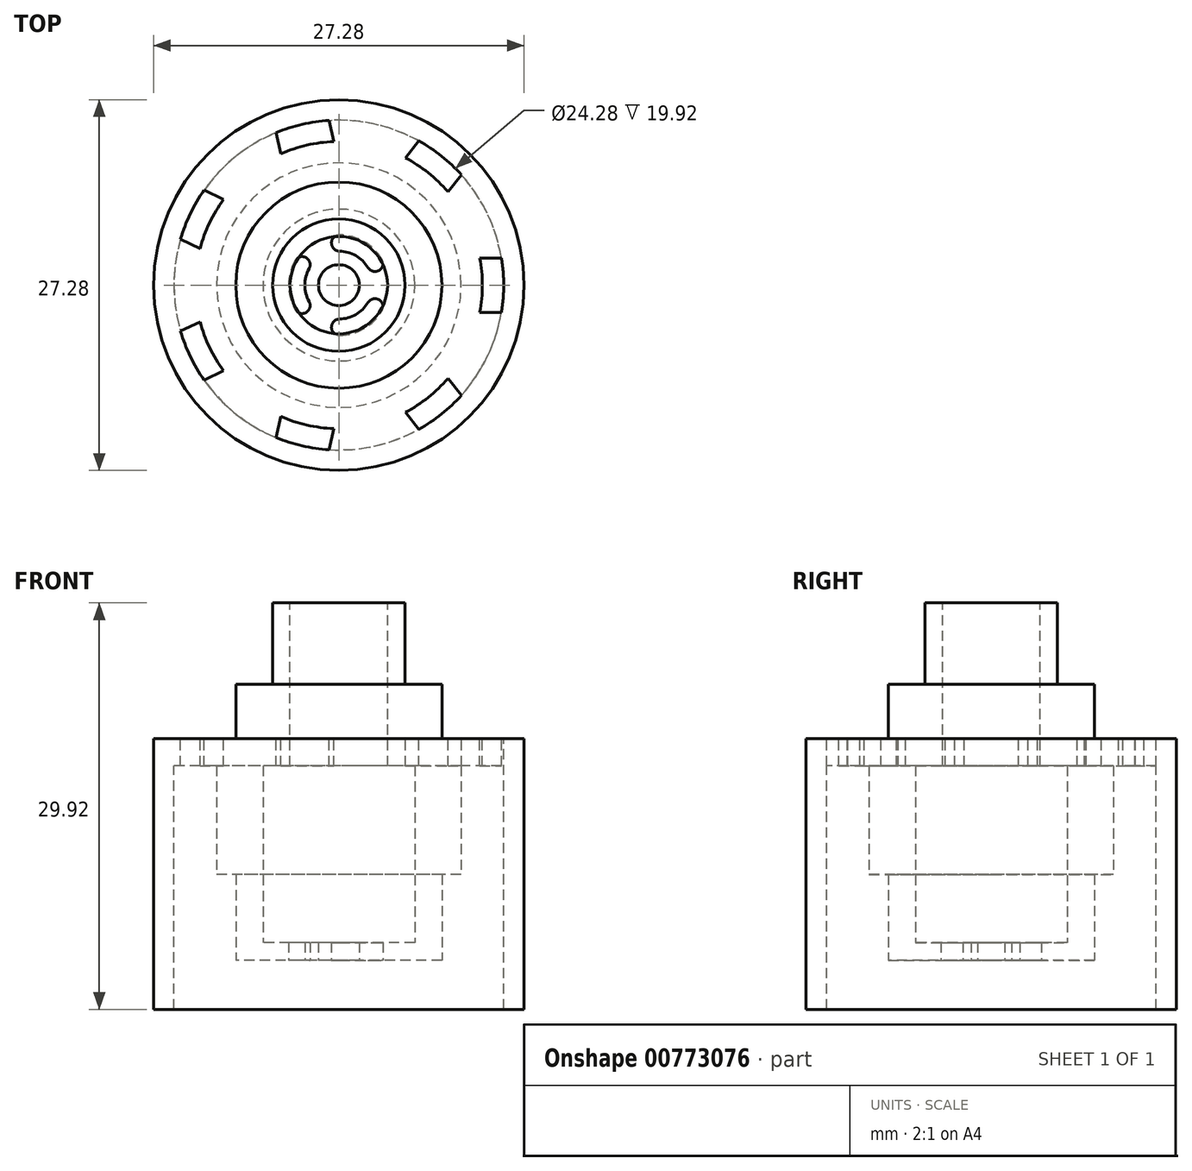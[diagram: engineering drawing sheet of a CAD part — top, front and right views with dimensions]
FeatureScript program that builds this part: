
annotation { "Feature Type Name" : "Feature", "Feature Type Description" : "" }
export const myFeature = defineFeature(function(context is Context, id is Id, definition is map)
    precondition{}
    {
        {
            var Q0;
            Q0=qCreatedBy(makeId("Top.planeOp"),FACE);
            var sketch = newSketch(context, id + "F0", { "sketchPlane" : qUnion([Q0])});
            skCircle(sketch, "E0", {"center": v(0, 0) * mm, "radius": 7.59 * mm});
            skCircle(sketch, "E1", {"center": v(0, 0) * mm, "radius": 1.5 * mm});
            skArc(sketch, "E2", {"start": v(2.14, 1.3) * mm, "mid": v(1.25, 2.17) * mm, "end": v(0.05, 2.5) * mm});
            skArc(sketch, "E3", {"start": v(3.17, 1.9) * mm, "mid": v(1.85, 3.2) * mm, "end": v(0.07, 3.7) * mm});
            skArc(sketch, "E4", {"start": v(2.14, 1.3) * mm, "mid": v(2.96, 1.09) * mm, "end": v(3.17, 1.9) * mm});
            skArc(sketch, "E5.MirrorC", {"start": v(2.14, -1.3) * mm, "mid": v(2.96, -1.09) * mm, "end": v(3.17, -1.9) * mm});
            skArc(sketch, "E6.1.0", {"start": v(-2.19, 1.2) * mm, "mid": v(-2.42, 2.02) * mm, "end": v(-3.24, 1.79) * mm});
            skArc(sketch, "E6.2.0", {"start": v(0.05, -2.5) * mm, "mid": v(-0.54, -3.11) * mm, "end": v(0.07, -3.7) * mm});
            skArc(sketch, "E7.1.0", {"start": v(0.05, 2.5) * mm, "mid": v(-0.54, 3.11) * mm, "end": v(0.07, 3.7) * mm});
            skArc(sketch, "E7.2.0", {"start": v(-2.19, -1.2) * mm, "mid": v(-2.42, -2.02) * mm, "end": v(-3.24, -1.79) * mm});
            skArc(sketch, "E8.trimOffspring", {"start": v(-2.19, 1.2) * mm, "mid": v(-2.5, 0) * mm, "end": v(-2.19, -1.2) * mm});
            skArc(sketch, "E9.trimOffspring", {"start": v(-3.24, 1.79) * mm, "mid": v(-3.7, 0) * mm, "end": v(-3.24, -1.79) * mm});
            skArc(sketch, "E10.trimOffspring", {"start": v(0.07, -3.7) * mm, "mid": v(1.85, -3.2) * mm, "end": v(3.17, -1.9) * mm});
            skArc(sketch, "E11.trimOffspring", {"start": v(0.05, -2.5) * mm, "mid": v(1.25, -2.17) * mm, "end": v(2.14, -1.3) * mm});
            skSolve(sketch);
        }
        {
            var Q0;
            Q0=makeQuery(id+"F0.imprint","IMPRINT",FACE,{"disambiguationData":[TD([[makeQuery(id+"F0.imprint","IMPRINT",EDGE,{"derivedFrom":sQuery(id+"F0.wireOp",EDGE,"E0")}),1.0]])]});
            extrude(context, id + "F1", {"entities" : qUnion([Q0]), "depth" : 1.32 * mm, "offsetDistance" : 25 * mm});
        }
        {
            var Q0;
            Q0=makeQuery(id+"F1.opExtrude","CAP_FACE",FACE,{"disambiguationData":[OSD([sQuery(id+"F0.wireOp",EDGE,"E0"),sQuery(id+"F0.wireOp",EDGE,"E1"),sQuery(id+"F0.wireOp",EDGE,"E2"),sQuery(id+"F0.wireOp",EDGE,"E3"),sQuery(id+"F0.wireOp",EDGE,"E4"),sQuery(id+"F0.wireOp",EDGE,"E5.MirrorC"),sQuery(id+"F0.wireOp",EDGE,"E6.1.0"),sQuery(id+"F0.wireOp",EDGE,"E6.2.0"),sQuery(id+"F0.wireOp",EDGE,"E7.1.0"),sQuery(id+"F0.wireOp",EDGE,"E7.2.0"),sQuery(id+"F0.wireOp",EDGE,"E8.trimOffspring"),sQuery(id+"F0.wireOp",EDGE,"E9.trimOffspring"),sQuery(id+"F0.wireOp",EDGE,"E10.trimOffspring"),sQuery(id+"F0.wireOp",EDGE,"E11.trimOffspring")])],"isStart":false});
            var sketch = newSketch(context, id + "F2", { "sketchPlane" : qUnion([Q0])});
            skCircle(sketch, "E12", {"center": v(0, 0) * mm, "radius": 5.59 * mm});
            skCircle(sketch, "E13", {"center": v(0, 0) * mm, "radius": 7.59 * mm});
            skSolve(sketch);
        }
        {
            var Q0;
            Q0=qSketchRegion(id+"F2",true);
            extrude(context, id + "F3", {"entities" : qUnion([Q0]), "operationType" : NewBodyOperationType.ADD, "depth" : 5 * mm, "offsetDistance" : 25 * mm});
        }
        {
            var Q0;
            Q0=makeQuery(id+"F3.opExtrude","CAP_FACE",FACE,{"disambiguationData":[OSD([sQuery(id+"F2.wireOp",EDGE,"E12"),sQuery(id+"F2.wireOp",EDGE,"E13")])],"isStart":false});
            var sketch = newSketch(context, id + "F4", { "sketchPlane" : qUnion([Q0])});
            skCircle(sketch, "E14", {"center": v(0, 0) * mm, "radius": 5.59 * mm});
            skCircle(sketch, "E15", {"center": v(0, 0) * mm, "radius": 9 * mm});
            skSolve(sketch);
        }
        {
            var Q0;
            Q0=qSketchRegion(id+"F4",true);
            extrude(context, id + "F5", {"entities" : qUnion([Q0]), "operationType" : NewBodyOperationType.ADD, "depth" : 10 * mm, "offsetDistance" : 25 * mm});
        }
        {
            var Q0;
            Q0=makeQuery(id+"F5.opExtrude","CAP_FACE",FACE,{"disambiguationData":[OSD([sQuery(id+"F4.wireOp",EDGE,"E14"),sQuery(id+"F4.wireOp",EDGE,"E15")])],"isStart":false});
            var sketch = newSketch(context, id + "F6", { "sketchPlane" : qUnion([Q0])});
            skCircle(sketch, "E16", {"center": v(0, 0) * mm, "radius": 3.59 * mm});
            skPoint(sketch, "E17.center", {"position": v(0, -0.02) * mm});
            skCircle(sketch, "E18", {"center": v(0, 0) * mm, "radius": 13.64 * mm});
            skSolve(sketch);
        }
        {
            var Q0;
            Q0=qSketchRegion(id+"F6",true);
            extrude(context, id + "F7", {"entities" : qUnion([Q0]), "operationType" : NewBodyOperationType.ADD, "oppositeDirection" : true, "depth" : 2 * mm, "offsetDistance" : 25 * mm});
        }
        {
            var Q0;
            Q0=makeQuery(id+"F7.opExtrude","CAP_FACE",FACE,{"disambiguationData":[OSD([sQuery(id+"F6.wireOp",EDGE,"l7Eqca51-6wLh-ttfN-njdu-v9geG0LM0wZP"),sQuery(id+"F6.wireOp",EDGE,"E16"),sQuery(id+"F6.wireOp",EDGE,"phvtgGP6-VrTs-5E6z-jD7F-d1pSkKgn639i"),sQuery(id+"F6.wireOp",EDGE,"hjbMQWua-LSD4-O8Im-Vq4h-WHBKtMpF6pe4"),sQuery(id+"F6.wireOp",EDGE,"E17.1.0"),sQuery(id+"F6.wireOp",EDGE,"E17.2.0"),sQuery(id+"F6.wireOp",EDGE,"df1b8ca7-3338-483b-9c3e-31f7fd8f63c8.1.0"),sQuery(id+"F6.wireOp",EDGE,"df1b8ca7-3338-483b-9c3e-31f7fd8f63c8.2.0"),sQuery(id+"F6.wireOp",EDGE,"y3VizclQ-A0cu-taS6-RFRV-s1O0MZUKXO3W"),sQuery(id+"F6.wireOp",EDGE,"1ec68f94-2945-48e9-9c7e-1afe0e5a7edd0.MirrorC"),sQuery(id+"F6.wireOp",EDGE,"db381333-0794-4eef-96fc-776305bcfc82.1.0"),sQuery(id+"F6.wireOp",EDGE,"db381333-0794-4eef-96fc-776305bcfc82.2.0"),sQuery(id+"F6.wireOp",EDGE,"c32bc6c7-bf0d-4e11-98ee-df4aab78b5ee.1.0"),sQuery(id+"F6.wireOp",EDGE,"c32bc6c7-bf0d-4e11-98ee-df4aab78b5ee.2.0"),sQuery(id+"F6.wireOp",EDGE,"d38ebc8d-960a-4b5c-9a9a-0cedfd8503cd.trimOffspring"),sQuery(id+"F6.wireOp",EDGE,"9424521c-a789-4a91-aaf5-1b38d683fb54.trimOffspring")])],"isStart":false});
            var sketch = newSketch(context, id + "F8", { "sketchPlane" : qUnion([Q0])});
            skCircle(sketch, "E19", {"center": v(0, 0) * mm, "radius": 12.14 * mm});
            skCircle(sketch, "E20.0", {"center": v(0, 0) * mm, "radius": 13.64 * mm});
            skSolve(sketch);
        }
        {
            var Q0;
            Q0=qSketchRegion(id+"F8",true);
            var Q1;
            Q1=qCreatedBy(makeId("Top.planeOp"),FACE);
            extrude(context, id + "F9", {"entities" : qUnion([Q0]), "operationType" : NewBodyOperationType.ADD, "endBound" : BoundingType.UP_TO_SURFACE, "depth" : 14.5 * mm, "endBoundEntityFace" : qUnion([Q1]), "hasOffset" : true, "offsetDistance" : 3.6 * mm, "offsetOppositeDirection" : true});
        }
        {
            var Q0;
            Q0=makeQuery(id+"F7.boolean.opBoolean","MERGE",FACE,{"derivedFrom":[makeQuery(id+"F5.opExtrude","CAP_FACE",FACE,{"disambiguationData":[OSD([sQuery(id+"F4.wireOp",EDGE,"E14"),sQuery(id+"F4.wireOp",EDGE,"E15")])],"isStart":false}),makeQuery(id+"F7.opExtrude","CAP_FACE",FACE,{"disambiguationData":[OSD([sQuery(id+"F6.wireOp",EDGE,"l7Eqca51-6wLh-ttfN-njdu-v9geG0LM0wZP"),sQuery(id+"F6.wireOp",EDGE,"E16"),sQuery(id+"F6.wireOp",EDGE,"phvtgGP6-VrTs-5E6z-jD7F-d1pSkKgn639i"),sQuery(id+"F6.wireOp",EDGE,"hjbMQWua-LSD4-O8Im-Vq4h-WHBKtMpF6pe4"),sQuery(id+"F6.wireOp",EDGE,"E17.1.0"),sQuery(id+"F6.wireOp",EDGE,"E17.2.0"),sQuery(id+"F6.wireOp",EDGE,"df1b8ca7-3338-483b-9c3e-31f7fd8f63c8.1.0"),sQuery(id+"F6.wireOp",EDGE,"df1b8ca7-3338-483b-9c3e-31f7fd8f63c8.2.0"),sQuery(id+"F6.wireOp",EDGE,"y3VizclQ-A0cu-taS6-RFRV-s1O0MZUKXO3W"),sQuery(id+"F6.wireOp",EDGE,"1ec68f94-2945-48e9-9c7e-1afe0e5a7edd0.MirrorC"),sQuery(id+"F6.wireOp",EDGE,"db381333-0794-4eef-96fc-776305bcfc82.1.0"),sQuery(id+"F6.wireOp",EDGE,"db381333-0794-4eef-96fc-776305bcfc82.2.0"),sQuery(id+"F6.wireOp",EDGE,"c32bc6c7-bf0d-4e11-98ee-df4aab78b5ee.1.0"),sQuery(id+"F6.wireOp",EDGE,"c32bc6c7-bf0d-4e11-98ee-df4aab78b5ee.2.0"),sQuery(id+"F6.wireOp",EDGE,"d38ebc8d-960a-4b5c-9a9a-0cedfd8503cd.trimOffspring"),sQuery(id+"F6.wireOp",EDGE,"9424521c-a789-4a91-aaf5-1b38d683fb54.trimOffspring")])],"isStart":true})]});
            var sketch = newSketch(context, id + "F10", { "sketchPlane" : qUnion([Q0])});
            skCircle(sketch, "E21", {"center": v(0, 0) * mm, "radius": 4.88 * mm});
            skCircle(sketch, "E22.0", {"center": v(0, 0) * mm, "radius": 3.59 * mm});
            skSolve(sketch);
        }
        {
            var Q0;
            Q0=qSketchRegion(id+"F10",true);
            extrude(context, id + "F11", {"entities" : qUnion([Q0]), "operationType" : NewBodyOperationType.ADD, "depth" : 10 * mm, "offsetDistance" : 25 * mm});
        }
        {
            var Q0;
            Q0=makeQuery(id+"F7.boolean.opBoolean","MERGE",FACE,{"derivedFrom":[makeQuery(id+"F5.opExtrude","CAP_FACE",FACE,{"disambiguationData":[OSD([sQuery(id+"F4.wireOp",EDGE,"E14"),sQuery(id+"F4.wireOp",EDGE,"E15")])],"isStart":false}),makeQuery(id+"F7.opExtrude","CAP_FACE",FACE,{"disambiguationData":[OSD([sQuery(id+"F6.wireOp",EDGE,"l7Eqca51-6wLh-ttfN-njdu-v9geG0LM0wZP"),sQuery(id+"F6.wireOp",EDGE,"E16"),sQuery(id+"F6.wireOp",EDGE,"phvtgGP6-VrTs-5E6z-jD7F-d1pSkKgn639i"),sQuery(id+"F6.wireOp",EDGE,"hjbMQWua-LSD4-O8Im-Vq4h-WHBKtMpF6pe4"),sQuery(id+"F6.wireOp",EDGE,"E17.1.0"),sQuery(id+"F6.wireOp",EDGE,"E17.2.0"),sQuery(id+"F6.wireOp",EDGE,"df1b8ca7-3338-483b-9c3e-31f7fd8f63c8.1.0"),sQuery(id+"F6.wireOp",EDGE,"df1b8ca7-3338-483b-9c3e-31f7fd8f63c8.2.0"),sQuery(id+"F6.wireOp",EDGE,"y3VizclQ-A0cu-taS6-RFRV-s1O0MZUKXO3W"),sQuery(id+"F6.wireOp",EDGE,"1ec68f94-2945-48e9-9c7e-1afe0e5a7edd0.MirrorC"),sQuery(id+"F6.wireOp",EDGE,"db381333-0794-4eef-96fc-776305bcfc82.1.0"),sQuery(id+"F6.wireOp",EDGE,"db381333-0794-4eef-96fc-776305bcfc82.2.0"),sQuery(id+"F6.wireOp",EDGE,"c32bc6c7-bf0d-4e11-98ee-df4aab78b5ee.1.0"),sQuery(id+"F6.wireOp",EDGE,"c32bc6c7-bf0d-4e11-98ee-df4aab78b5ee.2.0"),sQuery(id+"F6.wireOp",EDGE,"d38ebc8d-960a-4b5c-9a9a-0cedfd8503cd.trimOffspring"),sQuery(id+"F6.wireOp",EDGE,"9424521c-a789-4a91-aaf5-1b38d683fb54.trimOffspring")])],"isStart":true})]});
            var sketch = newSketch(context, id + "F12", { "sketchPlane" : qUnion([Q0])});
            skArc(sketch, "E23.0", {"start": v(11.97, -2) * mm, "mid": v(12.14, 0) * mm, "end": v(11.97, 2) * mm});
            skArc(sketch, "E24", {"start": v(10.38, -2) * mm, "mid": v(10.57, 0) * mm, "end": v(10.38, 2) * mm});
            skLineSegment(sketch, "E25", {"start": v(10.38, 2) * mm, "end": v(11.97, 2) * mm});
            skLineSegment(sketch, "E26.MirrorCS", {"start": v(10.38, -2) * mm, "end": v(11.97, -2) * mm});
            skArc(sketch, "E27.1.0", {"start": v(8.03, 6.87) * mm, "mid": v(6.59, 8.26) * mm, "end": v(4.9, 9.36) * mm});
            skLineSegment(sketch, "E27.1.1", {"start": v(8.03, 6.87) * mm, "end": v(9.03, 8.11) * mm});
            skLineSegment(sketch, "E27.1.2", {"start": v(4.9, 9.36) * mm, "end": v(5.9, 10.6) * mm});
            skArc(sketch, "E27.1.3", {"start": v(9.03, 8.11) * mm, "mid": v(7.57, 9.49) * mm, "end": v(5.9, 10.6) * mm});
            skArc(sketch, "E27.2.0", {"start": v(-0.36, 10.56) * mm, "mid": v(-2.35, 10.3) * mm, "end": v(-4.26, 9.67) * mm});
            skLineSegment(sketch, "E27.2.1", {"start": v(-0.36, 10.56) * mm, "end": v(-0.71, 12.12) * mm});
            skLineSegment(sketch, "E27.2.2", {"start": v(-4.26, 9.67) * mm, "end": v(-4.61, 11.23) * mm});
            skArc(sketch, "E27.2.3", {"start": v(-0.71, 12.12) * mm, "mid": v(-2.7, 11.83) * mm, "end": v(-4.61, 11.23) * mm});
            skArc(sketch, "E27.3.0", {"start": v(-8.48, 6.3) * mm, "mid": v(-9.52, 4.59) * mm, "end": v(-10.22, 2.7) * mm});
            skLineSegment(sketch, "E27.3.1", {"start": v(-8.48, 6.3) * mm, "end": v(-9.92, 7) * mm});
            skLineSegment(sketch, "E27.3.2", {"start": v(-10.22, 2.7) * mm, "end": v(-11.65, 3.4) * mm});
            skArc(sketch, "E27.3.3", {"start": v(-9.92, 7) * mm, "mid": v(-10.94, 5.27) * mm, "end": v(-11.65, 3.4) * mm});
            skArc(sketch, "E27.4.0", {"start": v(-10.22, -2.7) * mm, "mid": v(-9.52, -4.59) * mm, "end": v(-8.48, -6.3) * mm});
            skLineSegment(sketch, "E27.4.1", {"start": v(-10.22, -2.7) * mm, "end": v(-11.65, -3.4) * mm});
            skLineSegment(sketch, "E27.4.2", {"start": v(-8.48, -6.3) * mm, "end": v(-9.92, -7) * mm});
            skArc(sketch, "E27.4.3", {"start": v(-11.65, -3.4) * mm, "mid": v(-10.94, -5.27) * mm, "end": v(-9.92, -7) * mm});
            skArc(sketch, "E27.5.0", {"start": v(-4.26, -9.67) * mm, "mid": v(-2.35, -10.3) * mm, "end": v(-0.36, -10.56) * mm});
            skLineSegment(sketch, "E27.5.1", {"start": v(-4.26, -9.67) * mm, "end": v(-4.61, -11.23) * mm});
            skLineSegment(sketch, "E27.5.2", {"start": v(-0.36, -10.56) * mm, "end": v(-0.71, -12.12) * mm});
            skArc(sketch, "E27.5.3", {"start": v(-4.61, -11.23) * mm, "mid": v(-2.7, -11.83) * mm, "end": v(-0.71, -12.12) * mm});
            skArc(sketch, "E27.6.0", {"start": v(4.9, -9.36) * mm, "mid": v(6.59, -8.26) * mm, "end": v(8.03, -6.87) * mm});
            skLineSegment(sketch, "E27.6.1", {"start": v(4.9, -9.36) * mm, "end": v(5.9, -10.6) * mm});
            skLineSegment(sketch, "E27.6.2", {"start": v(8.03, -6.87) * mm, "end": v(9.03, -8.11) * mm});
            skArc(sketch, "E27.6.3", {"start": v(5.9, -10.6) * mm, "mid": v(7.57, -9.49) * mm, "end": v(9.03, -8.11) * mm});
            skSolve(sketch);
        }
        {
            var Q0;
            Q0=qSketchRegion(id+"F12",true);
            var Q1;
            {var subQ0=sQuery(id+"F6.wireOp",EDGE,"y3VizclQ-A0cu-taS6-RFRV-s1O0MZUKXO3W");var subQ1=sQuery(id+"F6.wireOp",EDGE,"df1b8ca7-3338-483b-9c3e-31f7fd8f63c8.1.0");var subQ2=sQuery(id+"F6.wireOp",EDGE,"E17.2.0");var subQ3=sQuery(id+"F6.wireOp",EDGE,"E17.1.0");var subQ4=sQuery(id+"F6.wireOp",EDGE,"df1b8ca7-3338-483b-9c3e-31f7fd8f63c8.2.0");var subQ5=sQuery(id+"F6.wireOp",EDGE,"db381333-0794-4eef-96fc-776305bcfc82.2.0");var subQ6=sQuery(id+"F6.wireOp",EDGE,"phvtgGP6-VrTs-5E6z-jD7F-d1pSkKgn639i");var subQ7=sQuery(id+"F6.wireOp",EDGE,"1ec68f94-2945-48e9-9c7e-1afe0e5a7edd0.MirrorC");var subQ8=sQuery(id+"F6.wireOp",EDGE,"l7Eqca51-6wLh-ttfN-njdu-v9geG0LM0wZP");var subQ9=sQuery(id+"F6.wireOp",EDGE,"hjbMQWua-LSD4-O8Im-Vq4h-WHBKtMpF6pe4");var subQ10=sQuery(id+"F6.wireOp",EDGE,"db381333-0794-4eef-96fc-776305bcfc82.1.0");var subQ11=sQuery(id+"F6.wireOp",EDGE,"c32bc6c7-bf0d-4e11-98ee-df4aab78b5ee.1.0");var subQ12=sQuery(id+"F6.wireOp",EDGE,"c32bc6c7-bf0d-4e11-98ee-df4aab78b5ee.2.0");var subQ13=sQuery(id+"F6.wireOp",EDGE,"d38ebc8d-960a-4b5c-9a9a-0cedfd8503cd.trimOffspring");var subQ14=sQuery(id+"F6.wireOp",EDGE,"9424521c-a789-4a91-aaf5-1b38d683fb54.trimOffspring");Q1=makeQuery(id+"F7.boolean.opBoolean","SPLIT",FACE,{"disambiguationData":[TD([makeQuery(id+"F5.opExtrude","SWEPT_FACE",FACE,{"disambiguationData":[OSD([sQuery(id+"F4.wireOp",EDGE,"E15")])]})])],"derivedFrom":makeQuery(id+"F7.opExtrude","CAP_FACE",FACE,{"disambiguationData":[OSD([subQ8,sQuery(id+"F6.wireOp",EDGE,"E16"),subQ6,subQ9,subQ3,subQ2,subQ1,subQ4,subQ0,subQ7,subQ10,subQ5,subQ11,subQ12,subQ13,subQ14])],"isStart":false})});}
            extrude(context, id + "F13", {"entities" : qUnion([Q0]), "operationType" : NewBodyOperationType.REMOVE, "oppositeDirection" : true, "depth" : 2 * mm, "endBoundEntityFace" : qUnion([Q1]), "offsetDistance" : 25 * mm});
        }
        {
            var Q0;
            Q0=makeQuery(id+"F9.opExtrude","CAP_FACE",FACE,{"disambiguationData":[OSD([sQuery(id+"F8.wireOp",EDGE,"E19"),sQuery(id+"F8.wireOp",EDGE,"E20.0")])],"isStart":false});
            var sketch = newSketch(context, id + "F14", { "sketchPlane" : qUnion([Q0])});
            skArc(sketch, "E28.0", {"start": v(-12.09, 1.1) * mm, "mid": v(-12.14, 0) * mm, "end": v(-12.09, -1.1) * mm});
            skArc(sketch, "E29", {"start": v(-11.9, -0.84) * mm, "mid": v(-11.26, 0) * mm, "end": v(-11.9, 0.84) * mm});
            skArc(sketch, "E30", {"start": v(-11.9, -0.84) * mm, "mid": v(-12.04, -0.94) * mm, "end": v(-12.09, -1.1) * mm});
            skArc(sketch, "E31.MirrorC", {"start": v(-11.9, 0.84) * mm, "mid": v(-12.04, 0.94) * mm, "end": v(-12.09, 1.1) * mm});
            skArc(sketch, "E32.1.0", {"start": v(-12.04, -1.52) * mm, "mid": v(-11.85, -2.6) * mm, "end": v(-11.57, -3.68) * mm});
            skArc(sketch, "E32.1.1", {"start": v(-11.45, -3.38) * mm, "mid": v(-11, -2.42) * mm, "end": v(-11.8, -1.74) * mm});
            skArc(sketch, "E32.1.2", {"start": v(-11.8, -1.74) * mm, "mid": v(-11.97, -1.67) * mm, "end": v(-12.04, -1.52) * mm});
            skArc(sketch, "E32.1.3", {"start": v(-11.45, -3.38) * mm, "mid": v(-11.56, -3.5) * mm, "end": v(-11.57, -3.68) * mm});
            skArc(sketch, "E32.2.0", {"start": v(-11.44, -4.07) * mm, "mid": v(-11.02, -5.1) * mm, "end": v(-10.5, -6.08) * mm});
            skArc(sketch, "E32.2.1", {"start": v(-10.45, -5.76) * mm, "mid": v(-10.22, -4.73) * mm, "end": v(-11.16, -4.23) * mm});
            skArc(sketch, "E32.2.2", {"start": v(-11.16, -4.23) * mm, "mid": v(-11.33, -4.2) * mm, "end": v(-11.44, -4.07) * mm});
            skArc(sketch, "E32.2.3", {"start": v(-10.45, -5.76) * mm, "mid": v(-10.54, -5.91) * mm, "end": v(-10.5, -6.08) * mm});
            skArc(sketch, "E32.3.0", {"start": v(-10.3, -6.43) * mm, "mid": v(-9.66, -7.35) * mm, "end": v(-8.95, -8.2) * mm});
            skArc(sketch, "E32.3.1", {"start": v(-8.97, -7.88) * mm, "mid": v(-8.97, -6.82) * mm, "end": v(-9.99, -6.53) * mm});
            skArc(sketch, "E32.3.2", {"start": v(-9.99, -6.53) * mm, "mid": v(-10.16, -6.54) * mm, "end": v(-10.3, -6.43) * mm});
            skArc(sketch, "E32.3.3", {"start": v(-8.97, -7.88) * mm, "mid": v(-9.02, -8.04) * mm, "end": v(-8.95, -8.2) * mm});
            skArc(sketch, "E32.4.0", {"start": v(-8.67, -8.5) * mm, "mid": v(-7.86, -9.25) * mm, "end": v(-6.98, -9.93) * mm});
            skArc(sketch, "E32.4.1", {"start": v(-7.06, -9.62) * mm, "mid": v(-7.3, -8.58) * mm, "end": v(-8.35, -8.53) * mm});
            skArc(sketch, "E32.4.2", {"start": v(-8.35, -8.53) * mm, "mid": v(-8.52, -8.57) * mm, "end": v(-8.67, -8.5) * mm});
            skArc(sketch, "E32.4.3", {"start": v(-7.06, -9.62) * mm, "mid": v(-7.08, -9.79) * mm, "end": v(-6.98, -9.93) * mm});
            skArc(sketch, "E32.5.0", {"start": v(-6.64, -10.16) * mm, "mid": v(-5.69, -10.72) * mm, "end": v(-4.68, -11.2) * mm});
            skArc(sketch, "E32.5.1", {"start": v(-4.83, -10.91) * mm, "mid": v(-5.28, -9.95) * mm, "end": v(-6.32, -10.12) * mm});
            skArc(sketch, "E32.5.2", {"start": v(-6.32, -10.12) * mm, "mid": v(-6.47, -10.2) * mm, "end": v(-6.64, -10.16) * mm});
            skArc(sketch, "E32.5.3", {"start": v(-4.83, -10.91) * mm, "mid": v(-4.8, -11.08) * mm, "end": v(-4.68, -11.2) * mm});
            skArc(sketch, "E32.6.0", {"start": v(-4.3, -11.35) * mm, "mid": v(-3.25, -11.7) * mm, "end": v(-2.17, -11.94) * mm});
            skArc(sketch, "E32.6.1", {"start": v(-2.37, -11.7) * mm, "mid": v(-3.01, -10.85) * mm, "end": v(-4, -11.25) * mm});
            skArc(sketch, "E32.6.2", {"start": v(-4, -11.25) * mm, "mid": v(-4.13, -11.35) * mm, "end": v(-4.3, -11.35) * mm});
            skArc(sketch, "E32.6.3", {"start": v(-2.37, -11.7) * mm, "mid": v(-2.31, -11.86) * mm, "end": v(-2.17, -11.94) * mm});
            skArc(sketch, "E32.7.0", {"start": v(-1.76, -12) * mm, "mid": v(-0.66, -12.12) * mm, "end": v(0.45, -12.13) * mm});
            skArc(sketch, "E32.7.1", {"start": v(0.2, -11.93) * mm, "mid": v(-0.6, -11.25) * mm, "end": v(-1.49, -11.84) * mm});
            skArc(sketch, "E32.7.2", {"start": v(-1.49, -11.84) * mm, "mid": v(-1.6, -11.98) * mm, "end": v(-1.76, -12) * mm});
            skArc(sketch, "E32.7.3", {"start": v(0.2, -11.93) * mm, "mid": v(0.29, -12.08) * mm, "end": v(0.45, -12.13) * mm});
            skArc(sketch, "E32.8.0", {"start": v(0.86, -12.1) * mm, "mid": v(1.96, -11.98) * mm, "end": v(3.05, -11.75) * mm});
            skArc(sketch, "E32.8.1", {"start": v(2.76, -11.61) * mm, "mid": v(1.82, -11.11) * mm, "end": v(1.1, -11.88) * mm});
            skArc(sketch, "E32.8.2", {"start": v(1.1, -11.88) * mm, "mid": v(1.02, -12.04) * mm, "end": v(0.86, -12.1) * mm});
            skArc(sketch, "E32.8.3", {"start": v(2.76, -11.61) * mm, "mid": v(2.88, -11.73) * mm, "end": v(3.05, -11.75) * mm});
            skArc(sketch, "E32.9.0", {"start": v(3.45, -11.64) * mm, "mid": v(4.5, -11.28) * mm, "end": v(5.5, -10.82) * mm});
            skArc(sketch, "E32.9.1", {"start": v(5.2, -10.75) * mm, "mid": v(4.17, -10.46) * mm, "end": v(3.62, -11.37) * mm});
            skArc(sketch, "E32.9.2", {"start": v(3.62, -11.37) * mm, "mid": v(3.58, -11.54) * mm, "end": v(3.45, -11.64) * mm});
            skArc(sketch, "E32.9.3", {"start": v(5.2, -10.75) * mm, "mid": v(5.33, -10.84) * mm, "end": v(5.5, -10.82) * mm});
            skArc(sketch, "E32.10.0", {"start": v(5.87, -10.63) * mm, "mid": v(6.81, -10.05) * mm, "end": v(7.7, -9.38) * mm});
            skArc(sketch, "E32.10.1", {"start": v(7.38, -9.38) * mm, "mid": v(6.32, -9.32) * mm, "end": v(5.98, -10.33) * mm});
            skArc(sketch, "E32.10.2", {"start": v(5.98, -10.33) * mm, "mid": v(5.98, -10.5) * mm, "end": v(5.87, -10.63) * mm});
            skArc(sketch, "E32.10.3", {"start": v(7.38, -9.38) * mm, "mid": v(7.54, -9.44) * mm, "end": v(7.7, -9.38) * mm});
            skArc(sketch, "E32.11.0", {"start": v(8.01, -9.12) * mm, "mid": v(8.81, -8.35) * mm, "end": v(9.54, -7.5) * mm});
            skArc(sketch, "E32.11.1", {"start": v(9.22, -7.57) * mm, "mid": v(8.18, -7.75) * mm, "end": v(8.06, -8.8) * mm});
            skArc(sketch, "E32.11.2", {"start": v(8.06, -8.8) * mm, "mid": v(8.1, -8.97) * mm, "end": v(8.01, -9.12) * mm});
            skArc(sketch, "E32.11.3", {"start": v(9.22, -7.57) * mm, "mid": v(9.4, -7.6) * mm, "end": v(9.54, -7.5) * mm});
            skArc(sketch, "E32.12.0", {"start": v(9.79, -7.18) * mm, "mid": v(10.4, -6.26) * mm, "end": v(10.93, -5.28) * mm});
            skArc(sketch, "E32.12.1", {"start": v(10.64, -5.41) * mm, "mid": v(9.65, -5.8) * mm, "end": v(9.77, -6.86) * mm});
            skArc(sketch, "E32.12.2", {"start": v(9.77, -6.86) * mm, "mid": v(9.83, -7.02) * mm, "end": v(9.79, -7.18) * mm});
            skArc(sketch, "E32.12.3", {"start": v(10.64, -5.41) * mm, "mid": v(10.8, -5.4) * mm, "end": v(10.93, -5.28) * mm});
            skArc(sketch, "E32.13.0", {"start": v(11.1, -4.9) * mm, "mid": v(11.5, -3.88) * mm, "end": v(11.8, -2.81) * mm});
            skArc(sketch, "E32.13.1", {"start": v(11.55, -3) * mm, "mid": v(10.67, -3.6) * mm, "end": v(11.01, -4.6) * mm});
            skArc(sketch, "E32.13.2", {"start": v(11.01, -4.6) * mm, "mid": v(11.11, -4.74) * mm, "end": v(11.1, -4.9) * mm});
            skArc(sketch, "E32.13.3", {"start": v(11.55, -3) * mm, "mid": v(11.71, -2.95) * mm, "end": v(11.8, -2.81) * mm});
            skArc(sketch, "E32.14.0", {"start": v(11.9, -2.4) * mm, "mid": v(12.07, -1.31) * mm, "end": v(12.14, -0.2) * mm});
            skArc(sketch, "E32.14.1", {"start": v(11.93, -0.45) * mm, "mid": v(11.2, -1.22) * mm, "end": v(11.74, -2.13) * mm});
            skArc(sketch, "E32.14.2", {"start": v(11.74, -2.13) * mm, "mid": v(11.87, -2.24) * mm, "end": v(11.9, -2.4) * mm});
            skArc(sketch, "E32.14.3", {"start": v(11.93, -0.45) * mm, "mid": v(12.08, -0.37) * mm, "end": v(12.14, -0.2) * mm});
            skArc(sketch, "E32.15.0", {"start": v(12.14, 0.2) * mm, "mid": v(12.07, 1.31) * mm, "end": v(11.9, 2.4) * mm});
            skArc(sketch, "E32.15.1", {"start": v(11.74, 2.13) * mm, "mid": v(11.2, 1.22) * mm, "end": v(11.93, 0.45) * mm});
            skArc(sketch, "E32.15.2", {"start": v(11.93, 0.45) * mm, "mid": v(12.08, 0.37) * mm, "end": v(12.14, 0.2) * mm});
            skArc(sketch, "E32.15.3", {"start": v(11.74, 2.13) * mm, "mid": v(11.87, 2.24) * mm, "end": v(11.9, 2.4) * mm});
            skArc(sketch, "E32.16.0", {"start": v(11.8, 2.81) * mm, "mid": v(11.5, 3.88) * mm, "end": v(11.1, 4.9) * mm});
            skArc(sketch, "E32.16.1", {"start": v(11.01, 4.6) * mm, "mid": v(10.67, 3.6) * mm, "end": v(11.55, 3) * mm});
            skArc(sketch, "E32.16.2", {"start": v(11.55, 3) * mm, "mid": v(11.71, 2.95) * mm, "end": v(11.8, 2.81) * mm});
            skArc(sketch, "E32.16.3", {"start": v(11.01, 4.6) * mm, "mid": v(11.11, 4.74) * mm, "end": v(11.1, 4.9) * mm});
            skArc(sketch, "E32.17.0", {"start": v(10.93, 5.28) * mm, "mid": v(10.4, 6.26) * mm, "end": v(9.79, 7.18) * mm});
            skArc(sketch, "E32.17.1", {"start": v(9.77, 6.86) * mm, "mid": v(9.65, 5.8) * mm, "end": v(10.64, 5.41) * mm});
            skArc(sketch, "E32.17.2", {"start": v(10.64, 5.41) * mm, "mid": v(10.8, 5.4) * mm, "end": v(10.93, 5.28) * mm});
            skArc(sketch, "E32.17.3", {"start": v(9.77, 6.86) * mm, "mid": v(9.83, 7.02) * mm, "end": v(9.79, 7.18) * mm});
            skArc(sketch, "E32.18.0", {"start": v(9.54, 7.5) * mm, "mid": v(8.81, 8.35) * mm, "end": v(8.01, 9.12) * mm});
            skArc(sketch, "E32.18.1", {"start": v(8.06, 8.8) * mm, "mid": v(8.18, 7.75) * mm, "end": v(9.22, 7.57) * mm});
            skArc(sketch, "E32.18.2", {"start": v(9.22, 7.57) * mm, "mid": v(9.4, 7.6) * mm, "end": v(9.54, 7.5) * mm});
            skArc(sketch, "E32.18.3", {"start": v(8.06, 8.8) * mm, "mid": v(8.1, 8.97) * mm, "end": v(8.01, 9.12) * mm});
            skArc(sketch, "E32.19.0", {"start": v(7.7, 9.38) * mm, "mid": v(6.81, 10.05) * mm, "end": v(5.87, 10.63) * mm});
            skArc(sketch, "E32.19.1", {"start": v(5.98, 10.33) * mm, "mid": v(6.32, 9.32) * mm, "end": v(7.38, 9.38) * mm});
            skArc(sketch, "E32.19.2", {"start": v(7.38, 9.38) * mm, "mid": v(7.54, 9.44) * mm, "end": v(7.7, 9.38) * mm});
            skArc(sketch, "E32.19.3", {"start": v(5.98, 10.33) * mm, "mid": v(5.98, 10.5) * mm, "end": v(5.87, 10.63) * mm});
            skArc(sketch, "E32.20.0", {"start": v(5.5, 10.82) * mm, "mid": v(4.5, 11.28) * mm, "end": v(3.45, 11.64) * mm});
            skArc(sketch, "E32.20.1", {"start": v(3.62, 11.37) * mm, "mid": v(4.17, 10.46) * mm, "end": v(5.2, 10.75) * mm});
            skArc(sketch, "E32.20.2", {"start": v(5.2, 10.75) * mm, "mid": v(5.33, 10.84) * mm, "end": v(5.5, 10.82) * mm});
            skArc(sketch, "E32.20.3", {"start": v(3.62, 11.37) * mm, "mid": v(3.58, 11.54) * mm, "end": v(3.45, 11.64) * mm});
            skArc(sketch, "E32.21.0", {"start": v(3.05, 11.75) * mm, "mid": v(1.96, 11.98) * mm, "end": v(0.86, 12.1) * mm});
            skArc(sketch, "E32.21.1", {"start": v(1.1, 11.88) * mm, "mid": v(1.82, 11.11) * mm, "end": v(2.76, 11.61) * mm});
            skArc(sketch, "E32.21.2", {"start": v(2.76, 11.61) * mm, "mid": v(2.88, 11.73) * mm, "end": v(3.05, 11.75) * mm});
            skArc(sketch, "E32.21.3", {"start": v(1.1, 11.88) * mm, "mid": v(1.02, 12.04) * mm, "end": v(0.86, 12.1) * mm});
            skArc(sketch, "E32.22.0", {"start": v(0.45, 12.13) * mm, "mid": v(-0.66, 12.12) * mm, "end": v(-1.76, 12) * mm});
            skArc(sketch, "E32.22.1", {"start": v(-1.49, 11.84) * mm, "mid": v(-0.6, 11.25) * mm, "end": v(0.2, 11.93) * mm});
            skArc(sketch, "E32.22.2", {"start": v(0.2, 11.93) * mm, "mid": v(0.29, 12.08) * mm, "end": v(0.45, 12.13) * mm});
            skArc(sketch, "E32.22.3", {"start": v(-1.49, 11.84) * mm, "mid": v(-1.6, 11.98) * mm, "end": v(-1.76, 12) * mm});
            skArc(sketch, "E32.23.0", {"start": v(-2.17, 11.94) * mm, "mid": v(-3.25, 11.7) * mm, "end": v(-4.3, 11.35) * mm});
            skArc(sketch, "E32.23.1", {"start": v(-4, 11.25) * mm, "mid": v(-3.01, 10.85) * mm, "end": v(-2.37, 11.7) * mm});
            skArc(sketch, "E32.23.2", {"start": v(-2.37, 11.7) * mm, "mid": v(-2.31, 11.86) * mm, "end": v(-2.17, 11.94) * mm});
            skArc(sketch, "E32.23.3", {"start": v(-4, 11.25) * mm, "mid": v(-4.13, 11.35) * mm, "end": v(-4.3, 11.35) * mm});
            skArc(sketch, "E32.24.0", {"start": v(-4.68, 11.2) * mm, "mid": v(-5.69, 10.72) * mm, "end": v(-6.64, 10.16) * mm});
            skArc(sketch, "E32.24.1", {"start": v(-6.32, 10.12) * mm, "mid": v(-5.28, 9.95) * mm, "end": v(-4.83, 10.91) * mm});
            skArc(sketch, "E32.24.2", {"start": v(-4.83, 10.91) * mm, "mid": v(-4.8, 11.08) * mm, "end": v(-4.68, 11.2) * mm});
            skArc(sketch, "E32.24.3", {"start": v(-6.32, 10.12) * mm, "mid": v(-6.47, 10.2) * mm, "end": v(-6.64, 10.16) * mm});
            skArc(sketch, "E32.25.0", {"start": v(-6.98, 9.93) * mm, "mid": v(-7.86, 9.25) * mm, "end": v(-8.67, 8.5) * mm});
            skArc(sketch, "E32.25.1", {"start": v(-8.35, 8.53) * mm, "mid": v(-7.3, 8.58) * mm, "end": v(-7.06, 9.62) * mm});
            skArc(sketch, "E32.25.2", {"start": v(-7.06, 9.62) * mm, "mid": v(-7.08, 9.79) * mm, "end": v(-6.98, 9.93) * mm});
            skArc(sketch, "E32.25.3", {"start": v(-8.35, 8.53) * mm, "mid": v(-8.52, 8.57) * mm, "end": v(-8.67, 8.5) * mm});
            skArc(sketch, "E32.26.0", {"start": v(-8.95, 8.2) * mm, "mid": v(-9.66, 7.35) * mm, "end": v(-10.3, 6.43) * mm});
            skArc(sketch, "E32.26.1", {"start": v(-9.99, 6.53) * mm, "mid": v(-8.97, 6.82) * mm, "end": v(-8.97, 7.88) * mm});
            skArc(sketch, "E32.26.2", {"start": v(-8.97, 7.88) * mm, "mid": v(-9.02, 8.04) * mm, "end": v(-8.95, 8.2) * mm});
            skArc(sketch, "E32.26.3", {"start": v(-9.99, 6.53) * mm, "mid": v(-10.16, 6.54) * mm, "end": v(-10.3, 6.43) * mm});
            skArc(sketch, "E32.27.0", {"start": v(-10.5, 6.08) * mm, "mid": v(-11.02, 5.1) * mm, "end": v(-11.44, 4.07) * mm});
            skArc(sketch, "E32.27.1", {"start": v(-11.16, 4.23) * mm, "mid": v(-10.22, 4.73) * mm, "end": v(-10.45, 5.76) * mm});
            skArc(sketch, "E32.27.2", {"start": v(-10.45, 5.76) * mm, "mid": v(-10.54, 5.91) * mm, "end": v(-10.5, 6.08) * mm});
            skArc(sketch, "E32.27.3", {"start": v(-11.16, 4.23) * mm, "mid": v(-11.33, 4.2) * mm, "end": v(-11.44, 4.07) * mm});
            skArc(sketch, "E32.28.0", {"start": v(-11.57, 3.68) * mm, "mid": v(-11.85, 2.6) * mm, "end": v(-12.04, 1.52) * mm});
            skArc(sketch, "E32.28.1", {"start": v(-11.8, 1.74) * mm, "mid": v(-11, 2.42) * mm, "end": v(-11.45, 3.38) * mm});
            skArc(sketch, "E32.28.2", {"start": v(-11.45, 3.38) * mm, "mid": v(-11.56, 3.5) * mm, "end": v(-11.57, 3.68) * mm});
            skArc(sketch, "E32.28.3", {"start": v(-11.8, 1.74) * mm, "mid": v(-11.97, 1.67) * mm, "end": v(-12.04, 1.52) * mm});
            skSolve(sketch);
        }
        {
            var Q0;
            Q0=makeQuery(id+"F7.boolean.opBoolean","MERGE",FACE,{"derivedFrom":[makeQuery(id+"F5.opExtrude","CAP_FACE",FACE,{"disambiguationData":[OSD([sQuery(id+"F4.wireOp",EDGE,"E14"),sQuery(id+"F4.wireOp",EDGE,"E15")])],"isStart":false}),makeQuery(id+"F7.opExtrude","CAP_FACE",FACE,{"disambiguationData":[OSD([sQuery(id+"F6.wireOp",EDGE,"l7Eqca51-6wLh-ttfN-njdu-v9geG0LM0wZP"),sQuery(id+"F6.wireOp",EDGE,"E16"),sQuery(id+"F6.wireOp",EDGE,"phvtgGP6-VrTs-5E6z-jD7F-d1pSkKgn639i"),sQuery(id+"F6.wireOp",EDGE,"hjbMQWua-LSD4-O8Im-Vq4h-WHBKtMpF6pe4"),sQuery(id+"F6.wireOp",EDGE,"E17.1.0"),sQuery(id+"F6.wireOp",EDGE,"E17.2.0"),sQuery(id+"F6.wireOp",EDGE,"df1b8ca7-3338-483b-9c3e-31f7fd8f63c8.1.0"),sQuery(id+"F6.wireOp",EDGE,"df1b8ca7-3338-483b-9c3e-31f7fd8f63c8.2.0"),sQuery(id+"F6.wireOp",EDGE,"y3VizclQ-A0cu-taS6-RFRV-s1O0MZUKXO3W"),sQuery(id+"F6.wireOp",EDGE,"1ec68f94-2945-48e9-9c7e-1afe0e5a7edd0.MirrorC"),sQuery(id+"F6.wireOp",EDGE,"db381333-0794-4eef-96fc-776305bcfc82.1.0"),sQuery(id+"F6.wireOp",EDGE,"db381333-0794-4eef-96fc-776305bcfc82.2.0"),sQuery(id+"F6.wireOp",EDGE,"c32bc6c7-bf0d-4e11-98ee-df4aab78b5ee.1.0"),sQuery(id+"F6.wireOp",EDGE,"c32bc6c7-bf0d-4e11-98ee-df4aab78b5ee.2.0"),sQuery(id+"F6.wireOp",EDGE,"d38ebc8d-960a-4b5c-9a9a-0cedfd8503cd.trimOffspring"),sQuery(id+"F6.wireOp",EDGE,"9424521c-a789-4a91-aaf5-1b38d683fb54.trimOffspring")])],"isStart":true})]});
            var sketch = newSketch(context, id + "F15", { "sketchPlane" : qUnion([Q0])});
            skCircle(sketch, "E33.0", {"center": v(0, 0) * mm, "radius": 4.88 * mm});
            skCircle(sketch, "E34", {"center": v(0, 0) * mm, "radius": 7.59 * mm});
            skSolve(sketch);
        }
        {
            var Q0;
            Q0=qSketchRegion(id+"F15",true);
            extrude(context, id + "F16", {"entities" : qUnion([Q0]), "operationType" : NewBodyOperationType.ADD, "depth" : 4 * mm, "offsetDistance" : 25 * mm});
        }
    });
